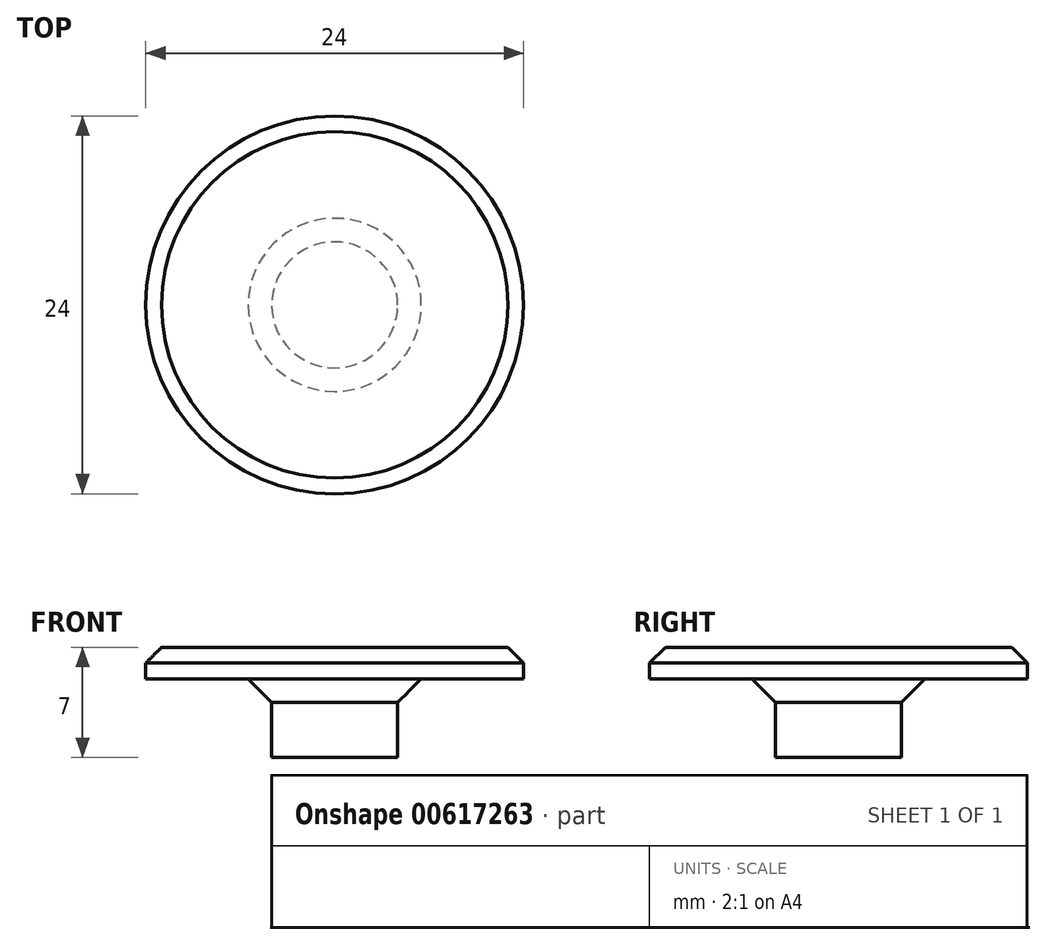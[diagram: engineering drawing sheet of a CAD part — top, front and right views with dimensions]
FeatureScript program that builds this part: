
annotation { "Feature Type Name" : "Feature", "Feature Type Description" : "" }
export const myFeature = defineFeature(function(context is Context, id is Id, definition is map)
    precondition{}
    {
        {
            var Q0;
            Q0=qCreatedBy(makeId("Front.planeOp"),FACE);
            var sketch = newSketch(context, id + "F0", { "sketchPlane" : qUnion([Q0])});
            skLineSegment(sketch, "E0", {"start": v(0, 0) * mm, "end": v(4, 0) * mm});
            skLineSegment(sketch, "E1", {"start": v(4, 0) * mm, "end": v(4, 3.5) * mm});
            skLineSegment(sketch, "E2", {"start": v(4, 3.5) * mm, "end": v(5.5, 5) * mm});
            skLineSegment(sketch, "E3", {"start": v(5.5, 5) * mm, "end": v(12, 5) * mm});
            skLineSegment(sketch, "E4", {"start": v(12, 5) * mm, "end": v(12, 7) * mm});
            skLineSegment(sketch, "E5", {"start": v(12, 7) * mm, "end": v(0, 7) * mm});
            skLineSegment(sketch, "E6", {"start": v(0, 7) * mm, "end": v(0, 0) * mm});
            skSolve(sketch);
        }
        {
            var Q0;
            Q0=makeQuery(id+"F0.imprint","IMPRINT",FACE,{"disambiguationData":[TD([[makeQuery(id+"F0.imprint","IMPRINT",EDGE,{"derivedFrom":sQuery(id+"F0.wireOp",EDGE,"E0")}),1.0]])]});
            var Q1;
            Q1=sQuery(id+"F0.wireOp",EDGE,"E6");
            revolve(context, id + "F1", {"entities" : qUnion([Q0]), "axis" : qUnion([Q1]), "revolveType" : RevolveType.FULL});
        }
        {
            var Q0;
            Q0=makeQuery(id+"F1.opRevolve","SWEPT_EDGE",EDGE,{"disambiguationData":[OSD([sQuery(id+"F0.wireOp",EDGE,"E4"),sQuery(id+"F0.wireOp",EDGE,"E5")])]});
            chamfer(context, id + "F2", {"entities" : qUnion([Q0]), "width" : 1 * mm, "tangentPropagation" : true});
        }
    });
